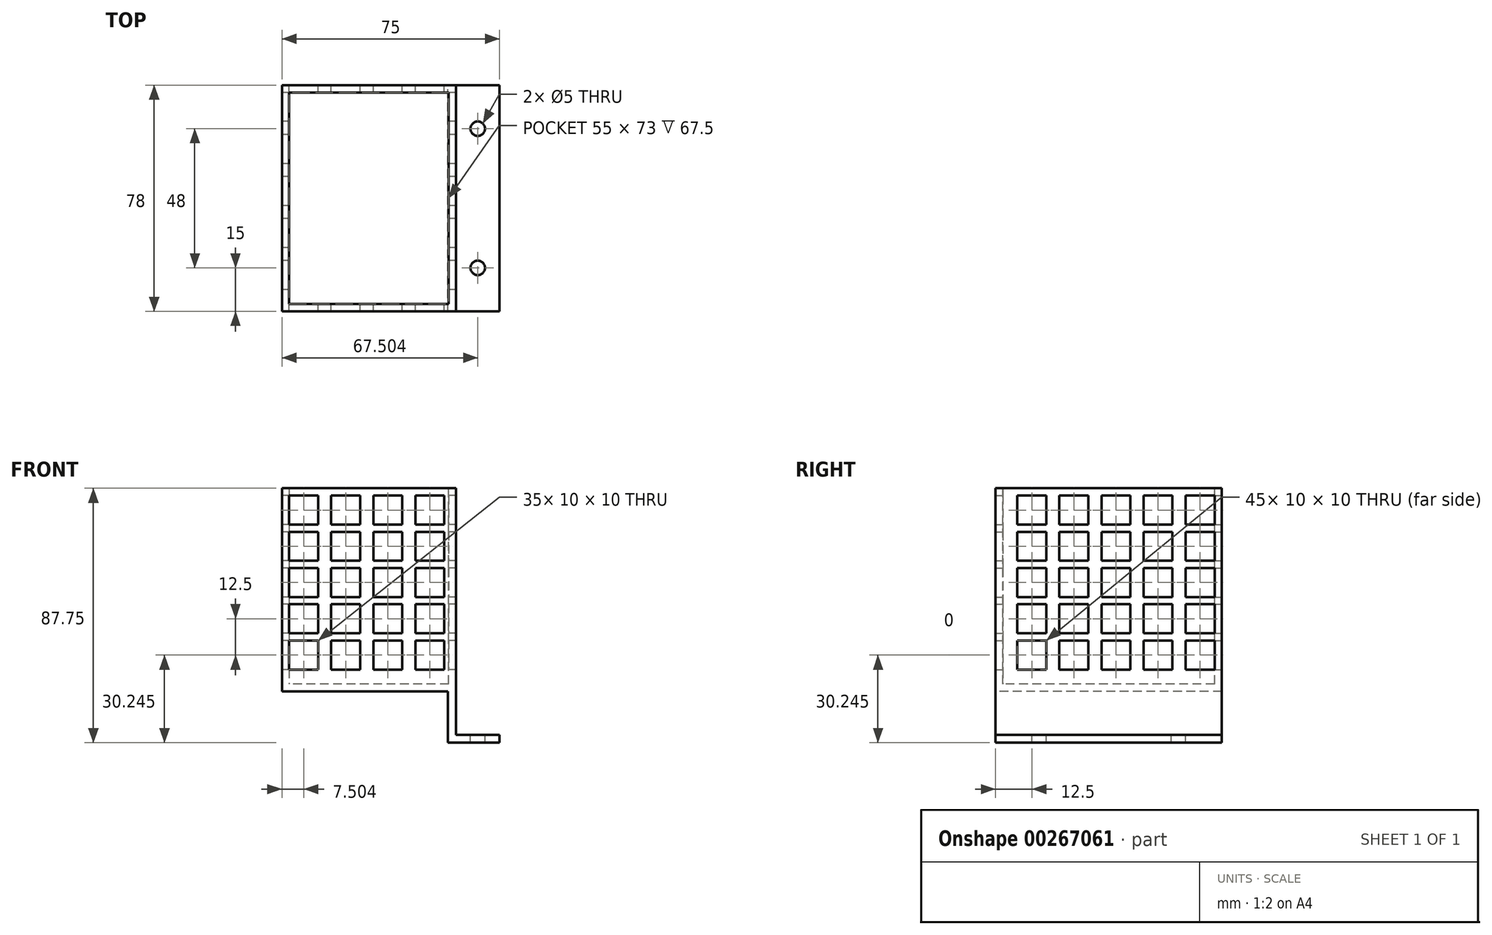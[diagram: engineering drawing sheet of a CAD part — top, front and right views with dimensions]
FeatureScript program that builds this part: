
annotation { "Feature Type Name" : "Feature", "Feature Type Description" : "" }
export const myFeature = defineFeature(function(context is Context, id is Id, definition is map)
    precondition{}
    {
        {
            var Q0;
            Q0=qCreatedBy(makeId("Front.planeOp"),FACE);
            var sketch = newSketch(context, id + "F0", { "sketchPlane" : qUnion([Q0])});
            skLineSegment(sketch, "E0", {"start": v(29.8, 18.38) * mm, "end": v(44.8, 18.38) * mm});
            skLineSegment(sketch, "E1", {"start": v(44.8, 18.38) * mm, "end": v(44.8, 21.13) * mm});
            skLineSegment(sketch, "E2", {"start": v(44.8, 21.13) * mm, "end": v(29.8, 21.13) * mm});
            skLineSegment(sketch, "E3", {"start": v(29.8, 21.13) * mm, "end": v(29.8, 18.38) * mm});
            skLineSegment(sketch, "E4.bottom", {"start": v(29.8, 18.38) * mm, "end": v(27.04, 18.38) * mm});
            skLineSegment(sketch, "E4.top", {"start": v(29.8, 36.13) * mm, "end": v(27.04, 36.13) * mm});
            skLineSegment(sketch, "E4.left", {"start": v(29.8, 18.38) * mm, "end": v(29.8, 36.13) * mm});
            skLineSegment(sketch, "E4.right", {"start": v(27.04, 18.38) * mm, "end": v(27.04, 36.13) * mm});
            skSolve(sketch);
        }
        {
            var Q0;
            Q0=qSketchRegion(id+"F0",true);
            extrude(context, id + "F1", {"entities" : qUnion([Q0]), "endBound" : BoundingType.SYMMETRIC, "depth" : 78 * mm});
        }
        {
            var Q0;
            Q0=makeQuery(id+"F1.opExtrude","SWEPT_FACE",FACE,{"disambiguationData":[OSD([sQuery(id+"F0.wireOp",EDGE,"E2")])]});
            var sketch = newSketch(context, id + "F2", { "sketchPlane" : qUnion([Q0])});
            skCircle(sketch, "E5", {"center": v(37.3, -24) * mm, "radius": 2.5 * mm});
            skCircle(sketch, "E6.0.1.0", {"center": v(37.3, 24) * mm, "radius": 2.5 * mm});
            skLineSegment(sketch, "E6.direction1", {"start": v(37.3, -24) * mm, "end": v(64.68, -24) * mm, "construction": true});
            skLineSegment(sketch, "E6.direction2", {"start": v(37.3, -24) * mm, "end": v(37.3, 24) * mm, "construction": true});
            skLineSegment(sketch, "E7.0", {"start": v(44.8, 39) * mm, "end": v(44.8, -39) * mm});
            skLineSegment(sketch, "E8.0", {"start": v(44.8, -39) * mm, "end": v(44.8, 39) * mm});
            skLineSegment(sketch, "E9", {"start": v(44.8, -1.08) * mm, "end": v(44.8, -1.08) * mm});
            skPoint(sketch, "E9.endSnap0", {"position": v(44.8, 0) * mm});
            skPoint(sketch, "E10", {"position": v(37.3, -1.08) * mm});
            skLineSegment(sketch, "E11", {"start": v(29.8, 0) * mm, "end": v(44.8, 0) * mm, "construction": true});
            skPoint(sketch, "E12", {"position": v(37.3, 0) * mm});
            skSolve(sketch);
        }
        {
            var Q0;
            Q0=makeQuery(id+"F2.imprint","IMPRINT",FACE,{"disambiguationData":[TD([[makeQuery(id+"F2.imprint","IMPRINT",EDGE,{"derivedFrom":sQuery(id+"F2.wireOp",EDGE,"E6.0.1.0")}),1.0]])]});
            var Q1;
            Q1=makeQuery(id+"F2.imprint","IMPRINT",FACE,{"disambiguationData":[TD([[makeQuery(id+"F2.imprint","IMPRINT",EDGE,{"derivedFrom":sQuery(id+"F2.wireOp",EDGE,"E5")}),1.0]])]});
            extrude(context, id + "F3", {"entities" : qUnion([Q0, Q1]), "operationType" : NewBodyOperationType.REMOVE, "endBound" : BoundingType.THROUGH_ALL, "oppositeDirection" : true, "depth" : 25 * mm});
        }
        {
            var Q0;
            Q0=makeQuery(id+"F1.opExtrude","SWEPT_FACE",FACE,{"disambiguationData":[OSD([sQuery(id+"F0.wireOp",EDGE,"E4.top")])]});
            var sketch = newSketch(context, id + "F4", { "sketchPlane" : qUnion([Q0])});
            skLineSegment(sketch, "E13", {"start": v(29.8, 39) * mm, "end": v(-30.2, 39) * mm});
            skLineSegment(sketch, "E14", {"start": v(29.8, -39) * mm, "end": v(-30.2, -39) * mm});
            skLineSegment(sketch, "E15", {"start": v(-30.2, 39) * mm, "end": v(-30.2, -39) * mm});
            skSolve(sketch);
        }
        {
            var Q0;
            {var subQ0=sQuery(id+"F4.wireOp",EDGE,"E13");Q0=makeQuery(id+"F4.imprint","IMPRINT",FACE,{"disambiguationData":[TD([[makeQuery(id+"F4.imprint","IMPRINT",EDGE,{"derivedFrom":subQ0}),1.0]])]});}
            extrude(context, id + "F5", {"entities" : qUnion([Q0]), "operationType" : NewBodyOperationType.ADD, "depth" : 70 * mm});
        }
        {
            var Q0;
            Q0=makeQuery(id+"F5.opExtrude","CAP_FACE",FACE,{"disambiguationData":[OSD([sQuery(id+"F0.wireOp",EDGE,"E0"),sQuery(id+"F0.wireOp",EDGE,"E3"),sQuery(id+"F4.wireOp",EDGE,"E13"),sQuery(id+"F4.wireOp",EDGE,"E14"),sQuery(id+"F4.wireOp",EDGE,"XroIyZZh-nZdX-ji37-o0S8-ZtPrHTp5OUbo")])],"isStart":false});
            shell(context, id + "F6", {"entities" : qUnion([Q0]), "thickness" : 2.5 * mm});
        }
        {
            var Q0;
            Q0=makeQuery(id+"F5.opExtrude","SWEPT_FACE",FACE,{"disambiguationData":[OSD([sQuery(id+"F4.wireOp",EDGE,"E13")])]});
            var sketch = newSketch(context, id + "F7", { "sketchPlane" : qUnion([Q0])});
            skLineSegment(sketch, "E16.bottom", {"start": v(17.7, 103.63) * mm, "end": v(27.7, 103.63) * mm});
            skLineSegment(sketch, "E16.top", {"start": v(17.7, 93.63) * mm, "end": v(27.7, 93.63) * mm});
            skLineSegment(sketch, "E16.left", {"start": v(27.7, 93.63) * mm, "end": v(27.7, 103.63) * mm});
            skLineSegment(sketch, "E16.right", {"start": v(17.7, 93.63) * mm, "end": v(17.7, 103.63) * mm});
            skLineSegment(sketch, "E17.0.1.0", {"start": v(17.7, 91.13) * mm, "end": v(27.7, 91.13) * mm});
            skLineSegment(sketch, "E17.0.1.1", {"start": v(27.7, 81.13) * mm, "end": v(27.7, 91.13) * mm});
            skLineSegment(sketch, "E17.0.1.2", {"start": v(17.7, 81.13) * mm, "end": v(17.7, 91.13) * mm});
            skLineSegment(sketch, "E17.0.1.3", {"start": v(17.7, 81.13) * mm, "end": v(27.7, 81.13) * mm});
            skLineSegment(sketch, "E17.0.2.0", {"start": v(17.7, 78.63) * mm, "end": v(27.7, 78.63) * mm});
            skLineSegment(sketch, "E17.0.2.1", {"start": v(27.7, 68.63) * mm, "end": v(27.7, 78.63) * mm});
            skLineSegment(sketch, "E17.0.2.2", {"start": v(17.7, 68.63) * mm, "end": v(17.7, 78.63) * mm});
            skLineSegment(sketch, "E17.0.2.3", {"start": v(17.7, 68.63) * mm, "end": v(27.7, 68.63) * mm});
            skLineSegment(sketch, "E17.0.3.0", {"start": v(17.7, 66.13) * mm, "end": v(27.7, 66.13) * mm});
            skLineSegment(sketch, "E17.0.3.1", {"start": v(27.7, 56.13) * mm, "end": v(27.7, 66.13) * mm});
            skLineSegment(sketch, "E17.0.3.2", {"start": v(17.7, 56.13) * mm, "end": v(17.7, 66.13) * mm});
            skLineSegment(sketch, "E17.0.3.3", {"start": v(17.7, 56.13) * mm, "end": v(27.7, 56.13) * mm});
            skLineSegment(sketch, "E17.0.4.0", {"start": v(17.7, 53.63) * mm, "end": v(27.7, 53.63) * mm});
            skLineSegment(sketch, "E17.0.4.1", {"start": v(27.7, 43.63) * mm, "end": v(27.7, 53.63) * mm});
            skLineSegment(sketch, "E17.0.4.2", {"start": v(17.7, 43.63) * mm, "end": v(17.7, 53.63) * mm});
            skLineSegment(sketch, "E17.0.4.3", {"start": v(17.7, 43.63) * mm, "end": v(27.7, 43.63) * mm});
            skLineSegment(sketch, "E18.1.0.0", {"start": v(3.2, 93.63) * mm, "end": v(3.2, 103.63) * mm});
            skLineSegment(sketch, "E18.1.0.1", {"start": v(3.2, 93.63) * mm, "end": v(13.2, 93.63) * mm});
            skLineSegment(sketch, "E18.1.0.2", {"start": v(3.2, 103.63) * mm, "end": v(13.2, 103.63) * mm});
            skLineSegment(sketch, "E18.1.0.3", {"start": v(13.2, 93.63) * mm, "end": v(13.2, 103.63) * mm});
            skLineSegment(sketch, "E18.1.1.0", {"start": v(3.2, 81.13) * mm, "end": v(3.2, 91.13) * mm});
            skLineSegment(sketch, "E18.1.1.1", {"start": v(3.2, 81.13) * mm, "end": v(13.2, 81.13) * mm});
            skLineSegment(sketch, "E18.1.1.2", {"start": v(3.2, 91.13) * mm, "end": v(13.2, 91.13) * mm});
            skLineSegment(sketch, "E18.1.1.3", {"start": v(13.2, 81.13) * mm, "end": v(13.2, 91.13) * mm});
            skLineSegment(sketch, "E18.1.2.0", {"start": v(3.2, 68.63) * mm, "end": v(3.2, 78.63) * mm});
            skLineSegment(sketch, "E18.1.2.1", {"start": v(3.2, 68.63) * mm, "end": v(13.2, 68.63) * mm});
            skLineSegment(sketch, "E18.1.2.2", {"start": v(3.2, 78.63) * mm, "end": v(13.2, 78.63) * mm});
            skLineSegment(sketch, "E18.1.2.3", {"start": v(13.2, 68.63) * mm, "end": v(13.2, 78.63) * mm});
            skLineSegment(sketch, "E18.1.3.0", {"start": v(3.2, 56.13) * mm, "end": v(3.2, 66.13) * mm});
            skLineSegment(sketch, "E18.1.3.1", {"start": v(3.2, 56.13) * mm, "end": v(13.2, 56.13) * mm});
            skLineSegment(sketch, "E18.1.3.2", {"start": v(3.2, 66.13) * mm, "end": v(13.2, 66.13) * mm});
            skLineSegment(sketch, "E18.1.3.3", {"start": v(13.2, 56.13) * mm, "end": v(13.2, 66.13) * mm});
            skLineSegment(sketch, "E18.1.4.0", {"start": v(3.2, 43.63) * mm, "end": v(3.2, 53.63) * mm});
            skLineSegment(sketch, "E18.1.4.1", {"start": v(3.2, 43.63) * mm, "end": v(13.2, 43.63) * mm});
            skLineSegment(sketch, "E18.1.4.2", {"start": v(3.2, 53.63) * mm, "end": v(13.2, 53.63) * mm});
            skLineSegment(sketch, "E18.1.4.3", {"start": v(13.2, 43.63) * mm, "end": v(13.2, 53.63) * mm});
            skLineSegment(sketch, "E18.2.0.0", {"start": v(-11.3, 93.63) * mm, "end": v(-11.3, 103.63) * mm});
            skLineSegment(sketch, "E18.2.0.1", {"start": v(-11.3, 93.63) * mm, "end": v(-1.3, 93.63) * mm});
            skLineSegment(sketch, "E18.2.0.2", {"start": v(-11.3, 103.63) * mm, "end": v(-1.3, 103.63) * mm});
            skLineSegment(sketch, "E18.2.0.3", {"start": v(-1.3, 93.63) * mm, "end": v(-1.3, 103.63) * mm});
            skLineSegment(sketch, "E18.2.1.0", {"start": v(-11.3, 81.13) * mm, "end": v(-11.3, 91.13) * mm});
            skLineSegment(sketch, "E18.2.1.1", {"start": v(-11.3, 81.13) * mm, "end": v(-1.3, 81.13) * mm});
            skLineSegment(sketch, "E18.2.1.2", {"start": v(-11.3, 91.13) * mm, "end": v(-1.3, 91.13) * mm});
            skLineSegment(sketch, "E18.2.1.3", {"start": v(-1.3, 81.13) * mm, "end": v(-1.3, 91.13) * mm});
            skLineSegment(sketch, "E18.2.2.0", {"start": v(-11.3, 68.63) * mm, "end": v(-11.3, 78.63) * mm});
            skLineSegment(sketch, "E18.2.2.1", {"start": v(-11.3, 68.63) * mm, "end": v(-1.3, 68.63) * mm});
            skLineSegment(sketch, "E18.2.2.2", {"start": v(-11.3, 78.63) * mm, "end": v(-1.3, 78.63) * mm});
            skLineSegment(sketch, "E18.2.2.3", {"start": v(-1.3, 68.63) * mm, "end": v(-1.3, 78.63) * mm});
            skLineSegment(sketch, "E18.2.3.0", {"start": v(-11.3, 56.13) * mm, "end": v(-11.3, 66.13) * mm});
            skLineSegment(sketch, "E18.2.3.1", {"start": v(-11.3, 56.13) * mm, "end": v(-1.3, 56.13) * mm});
            skLineSegment(sketch, "E18.2.3.2", {"start": v(-11.3, 66.13) * mm, "end": v(-1.3, 66.13) * mm});
            skLineSegment(sketch, "E18.2.3.3", {"start": v(-1.3, 56.13) * mm, "end": v(-1.3, 66.13) * mm});
            skLineSegment(sketch, "E18.2.4.0", {"start": v(-11.3, 43.63) * mm, "end": v(-11.3, 53.63) * mm});
            skLineSegment(sketch, "E18.2.4.1", {"start": v(-11.3, 43.63) * mm, "end": v(-1.3, 43.63) * mm});
            skLineSegment(sketch, "E18.2.4.2", {"start": v(-11.3, 53.63) * mm, "end": v(-1.3, 53.63) * mm});
            skLineSegment(sketch, "E18.2.4.3", {"start": v(-1.3, 43.63) * mm, "end": v(-1.3, 53.63) * mm});
            skLineSegment(sketch, "E18.3.0.0", {"start": v(-25.8, 93.63) * mm, "end": v(-25.8, 103.63) * mm});
            skLineSegment(sketch, "E18.3.0.1", {"start": v(-25.8, 93.63) * mm, "end": v(-15.8, 93.63) * mm});
            skLineSegment(sketch, "E18.3.0.2", {"start": v(-25.8, 103.63) * mm, "end": v(-15.8, 103.63) * mm});
            skLineSegment(sketch, "E18.3.0.3", {"start": v(-15.8, 93.63) * mm, "end": v(-15.8, 103.63) * mm});
            skLineSegment(sketch, "E18.3.1.0", {"start": v(-25.8, 81.13) * mm, "end": v(-25.8, 91.13) * mm});
            skLineSegment(sketch, "E18.3.1.1", {"start": v(-25.8, 81.13) * mm, "end": v(-15.8, 81.13) * mm});
            skLineSegment(sketch, "E18.3.1.2", {"start": v(-25.8, 91.13) * mm, "end": v(-15.8, 91.13) * mm});
            skLineSegment(sketch, "E18.3.1.3", {"start": v(-15.8, 81.13) * mm, "end": v(-15.8, 91.13) * mm});
            skLineSegment(sketch, "E18.3.2.0", {"start": v(-25.8, 68.63) * mm, "end": v(-25.8, 78.63) * mm});
            skLineSegment(sketch, "E18.3.2.1", {"start": v(-25.8, 68.63) * mm, "end": v(-15.8, 68.63) * mm});
            skLineSegment(sketch, "E18.3.2.2", {"start": v(-25.8, 78.63) * mm, "end": v(-15.8, 78.63) * mm});
            skLineSegment(sketch, "E18.3.2.3", {"start": v(-15.8, 68.63) * mm, "end": v(-15.8, 78.63) * mm});
            skLineSegment(sketch, "E18.3.3.0", {"start": v(-25.8, 56.13) * mm, "end": v(-25.8, 66.13) * mm});
            skLineSegment(sketch, "E18.3.3.1", {"start": v(-25.8, 56.13) * mm, "end": v(-15.8, 56.13) * mm});
            skLineSegment(sketch, "E18.3.3.2", {"start": v(-25.8, 66.13) * mm, "end": v(-15.8, 66.13) * mm});
            skLineSegment(sketch, "E18.3.3.3", {"start": v(-15.8, 56.13) * mm, "end": v(-15.8, 66.13) * mm});
            skLineSegment(sketch, "E18.3.4.0", {"start": v(-25.8, 43.63) * mm, "end": v(-25.8, 53.63) * mm});
            skLineSegment(sketch, "E18.3.4.1", {"start": v(-25.8, 43.63) * mm, "end": v(-15.8, 43.63) * mm});
            skLineSegment(sketch, "E18.3.4.2", {"start": v(-25.8, 53.63) * mm, "end": v(-15.8, 53.63) * mm});
            skLineSegment(sketch, "E18.3.4.3", {"start": v(-15.8, 43.63) * mm, "end": v(-15.8, 53.63) * mm});
            skLineSegment(sketch, "E18.direction1", {"start": v(17.7, 93.63) * mm, "end": v(3.2, 93.63) * mm, "construction": true});
            skLineSegment(sketch, "E18.direction2", {"start": v(17.7, 93.63) * mm, "end": v(17.7, 81.13) * mm, "construction": true});
            skSolve(sketch);
        }
        {
            var Q0;
            Q0 = qSketchRegion(id + "F7", true);
            extrude(context, id + "F8", {"entities" : qUnion([Q0]), "operationType" : NewBodyOperationType.REMOVE, "endBound" : BoundingType.THROUGH_ALL, "oppositeDirection" : true, "depth" : 25 * mm});
        }
        {
            var Q0;
            Q0=makeQuery(id+"F5.opExtrude","SWEPT_FACE",FACE,{"disambiguationData":[OSD([sQuery(id+"F4.wireOp",EDGE,"E15")])]});
            var sketch = newSketch(context, id + "F9", { "sketchPlane" : qUnion([Q0])});
            skLineSegment(sketch, "E19.bottom", {"start": v(-36.5, 103.63) * mm, "end": v(-26.5, 103.63) * mm});
            skLineSegment(sketch, "E19.top", {"start": v(-36.5, 93.63) * mm, "end": v(-26.5, 93.63) * mm});
            skLineSegment(sketch, "E19.left", {"start": v(-36.5, 103.63) * mm, "end": v(-36.5, 93.63) * mm});
            skLineSegment(sketch, "E19.right", {"start": v(-26.5, 103.63) * mm, "end": v(-26.5, 93.63) * mm});
            skLineSegment(sketch, "E20.0.1.0", {"start": v(-36.5, 91.13) * mm, "end": v(-36.5, 81.13) * mm});
            skLineSegment(sketch, "E20.0.1.1", {"start": v(-36.5, 91.13) * mm, "end": v(-26.5, 91.13) * mm});
            skLineSegment(sketch, "E20.0.1.2", {"start": v(-26.5, 91.13) * mm, "end": v(-26.5, 81.13) * mm});
            skLineSegment(sketch, "E20.0.1.3", {"start": v(-36.5, 81.13) * mm, "end": v(-26.5, 81.13) * mm});
            skLineSegment(sketch, "E20.0.2.0", {"start": v(-36.5, 78.63) * mm, "end": v(-36.5, 68.63) * mm});
            skLineSegment(sketch, "E20.0.2.1", {"start": v(-36.5, 78.63) * mm, "end": v(-26.5, 78.63) * mm});
            skLineSegment(sketch, "E20.0.2.2", {"start": v(-26.5, 78.63) * mm, "end": v(-26.5, 68.63) * mm});
            skLineSegment(sketch, "E20.0.2.3", {"start": v(-36.5, 68.63) * mm, "end": v(-26.5, 68.63) * mm});
            skLineSegment(sketch, "E20.0.3.0", {"start": v(-36.5, 66.13) * mm, "end": v(-36.5, 56.13) * mm});
            skLineSegment(sketch, "E20.0.3.1", {"start": v(-36.5, 66.13) * mm, "end": v(-26.5, 66.13) * mm});
            skLineSegment(sketch, "E20.0.3.2", {"start": v(-26.5, 66.13) * mm, "end": v(-26.5, 56.13) * mm});
            skLineSegment(sketch, "E20.0.3.3", {"start": v(-36.5, 56.13) * mm, "end": v(-26.5, 56.13) * mm});
            skLineSegment(sketch, "E20.0.4.0", {"start": v(-36.5, 53.63) * mm, "end": v(-36.5, 43.63) * mm});
            skLineSegment(sketch, "E20.0.4.1", {"start": v(-36.5, 53.63) * mm, "end": v(-26.5, 53.63) * mm});
            skLineSegment(sketch, "E20.0.4.2", {"start": v(-26.5, 53.63) * mm, "end": v(-26.5, 43.63) * mm});
            skLineSegment(sketch, "E20.0.4.3", {"start": v(-36.5, 43.63) * mm, "end": v(-26.5, 43.63) * mm});
            skLineSegment(sketch, "E20.1.0.0", {"start": v(-22, 103.63) * mm, "end": v(-22, 93.63) * mm});
            skLineSegment(sketch, "E20.1.0.1", {"start": v(-22, 103.63) * mm, "end": v(-12, 103.63) * mm});
            skLineSegment(sketch, "E20.1.0.2", {"start": v(-12, 103.63) * mm, "end": v(-12, 93.63) * mm});
            skLineSegment(sketch, "E20.1.0.3", {"start": v(-22, 93.63) * mm, "end": v(-12, 93.63) * mm});
            skLineSegment(sketch, "E20.1.1.0", {"start": v(-22, 91.13) * mm, "end": v(-22, 81.13) * mm});
            skLineSegment(sketch, "E20.1.1.1", {"start": v(-22, 91.13) * mm, "end": v(-12, 91.13) * mm});
            skLineSegment(sketch, "E20.1.1.2", {"start": v(-12, 91.13) * mm, "end": v(-12, 81.13) * mm});
            skLineSegment(sketch, "E20.1.1.3", {"start": v(-22, 81.13) * mm, "end": v(-12, 81.13) * mm});
            skLineSegment(sketch, "E20.1.2.0", {"start": v(-22, 78.63) * mm, "end": v(-22, 68.63) * mm});
            skLineSegment(sketch, "E20.1.2.1", {"start": v(-22, 78.63) * mm, "end": v(-12, 78.63) * mm});
            skLineSegment(sketch, "E20.1.2.2", {"start": v(-12, 78.63) * mm, "end": v(-12, 68.63) * mm});
            skLineSegment(sketch, "E20.1.2.3", {"start": v(-22, 68.63) * mm, "end": v(-12, 68.63) * mm});
            skLineSegment(sketch, "E20.1.3.0", {"start": v(-22, 66.13) * mm, "end": v(-22, 56.13) * mm});
            skLineSegment(sketch, "E20.1.3.1", {"start": v(-22, 66.13) * mm, "end": v(-12, 66.13) * mm});
            skLineSegment(sketch, "E20.1.3.2", {"start": v(-12, 66.13) * mm, "end": v(-12, 56.13) * mm});
            skLineSegment(sketch, "E20.1.3.3", {"start": v(-22, 56.13) * mm, "end": v(-12, 56.13) * mm});
            skLineSegment(sketch, "E20.1.4.0", {"start": v(-22, 53.63) * mm, "end": v(-22, 43.63) * mm});
            skLineSegment(sketch, "E20.1.4.1", {"start": v(-22, 53.63) * mm, "end": v(-12, 53.63) * mm});
            skLineSegment(sketch, "E20.1.4.2", {"start": v(-12, 53.63) * mm, "end": v(-12, 43.63) * mm});
            skLineSegment(sketch, "E20.1.4.3", {"start": v(-22, 43.63) * mm, "end": v(-12, 43.63) * mm});
            skLineSegment(sketch, "E20.2.0.0", {"start": v(-7.5, 103.63) * mm, "end": v(-7.5, 93.63) * mm});
            skLineSegment(sketch, "E20.2.0.1", {"start": v(-7.5, 103.63) * mm, "end": v(2.5, 103.63) * mm});
            skLineSegment(sketch, "E20.2.0.2", {"start": v(2.5, 103.63) * mm, "end": v(2.5, 93.63) * mm});
            skLineSegment(sketch, "E20.2.0.3", {"start": v(-7.5, 93.63) * mm, "end": v(2.5, 93.63) * mm});
            skLineSegment(sketch, "E20.2.1.0", {"start": v(-7.5, 91.13) * mm, "end": v(-7.5, 81.13) * mm});
            skLineSegment(sketch, "E20.2.1.1", {"start": v(-7.5, 91.13) * mm, "end": v(2.5, 91.13) * mm});
            skLineSegment(sketch, "E20.2.1.2", {"start": v(2.5, 91.13) * mm, "end": v(2.5, 81.13) * mm});
            skLineSegment(sketch, "E20.2.1.3", {"start": v(-7.5, 81.13) * mm, "end": v(2.5, 81.13) * mm});
            skLineSegment(sketch, "E20.2.2.0", {"start": v(-7.5, 78.63) * mm, "end": v(-7.5, 68.63) * mm});
            skLineSegment(sketch, "E20.2.2.1", {"start": v(-7.5, 78.63) * mm, "end": v(2.5, 78.63) * mm});
            skLineSegment(sketch, "E20.2.2.2", {"start": v(2.5, 78.63) * mm, "end": v(2.5, 68.63) * mm});
            skLineSegment(sketch, "E20.2.2.3", {"start": v(-7.5, 68.63) * mm, "end": v(2.5, 68.63) * mm});
            skLineSegment(sketch, "E20.2.3.0", {"start": v(-7.5, 66.13) * mm, "end": v(-7.5, 56.13) * mm});
            skLineSegment(sketch, "E20.2.3.1", {"start": v(-7.5, 66.13) * mm, "end": v(2.5, 66.13) * mm});
            skLineSegment(sketch, "E20.2.3.2", {"start": v(2.5, 66.13) * mm, "end": v(2.5, 56.13) * mm});
            skLineSegment(sketch, "E20.2.3.3", {"start": v(-7.5, 56.13) * mm, "end": v(2.5, 56.13) * mm});
            skLineSegment(sketch, "E20.2.4.0", {"start": v(-7.5, 53.63) * mm, "end": v(-7.5, 43.63) * mm});
            skLineSegment(sketch, "E20.2.4.1", {"start": v(-7.5, 53.63) * mm, "end": v(2.5, 53.63) * mm});
            skLineSegment(sketch, "E20.2.4.2", {"start": v(2.5, 53.63) * mm, "end": v(2.5, 43.63) * mm});
            skLineSegment(sketch, "E20.2.4.3", {"start": v(-7.5, 43.63) * mm, "end": v(2.5, 43.63) * mm});
            skLineSegment(sketch, "E20.3.0.0", {"start": v(7, 103.63) * mm, "end": v(7, 93.63) * mm});
            skLineSegment(sketch, "E20.3.0.1", {"start": v(7, 103.63) * mm, "end": v(17, 103.63) * mm});
            skLineSegment(sketch, "E20.3.0.2", {"start": v(17, 103.63) * mm, "end": v(17, 93.63) * mm});
            skLineSegment(sketch, "E20.3.0.3", {"start": v(7, 93.63) * mm, "end": v(17, 93.63) * mm});
            skLineSegment(sketch, "E20.3.1.0", {"start": v(7, 91.13) * mm, "end": v(7, 81.13) * mm});
            skLineSegment(sketch, "E20.3.1.1", {"start": v(7, 91.13) * mm, "end": v(17, 91.13) * mm});
            skLineSegment(sketch, "E20.3.1.2", {"start": v(17, 91.13) * mm, "end": v(17, 81.13) * mm});
            skLineSegment(sketch, "E20.3.1.3", {"start": v(7, 81.13) * mm, "end": v(17, 81.13) * mm});
            skLineSegment(sketch, "E20.3.2.0", {"start": v(7, 78.63) * mm, "end": v(7, 68.63) * mm});
            skLineSegment(sketch, "E20.3.2.1", {"start": v(7, 78.63) * mm, "end": v(17, 78.63) * mm});
            skLineSegment(sketch, "E20.3.2.2", {"start": v(17, 78.63) * mm, "end": v(17, 68.63) * mm});
            skLineSegment(sketch, "E20.3.2.3", {"start": v(7, 68.63) * mm, "end": v(17, 68.63) * mm});
            skLineSegment(sketch, "E20.3.3.0", {"start": v(7, 66.13) * mm, "end": v(7, 56.13) * mm});
            skLineSegment(sketch, "E20.3.3.1", {"start": v(7, 66.13) * mm, "end": v(17, 66.13) * mm});
            skLineSegment(sketch, "E20.3.3.2", {"start": v(17, 66.13) * mm, "end": v(17, 56.13) * mm});
            skLineSegment(sketch, "E20.3.3.3", {"start": v(7, 56.13) * mm, "end": v(17, 56.13) * mm});
            skLineSegment(sketch, "E20.3.4.0", {"start": v(7, 53.63) * mm, "end": v(7, 43.63) * mm});
            skLineSegment(sketch, "E20.3.4.1", {"start": v(7, 53.63) * mm, "end": v(17, 53.63) * mm});
            skLineSegment(sketch, "E20.3.4.2", {"start": v(17, 53.63) * mm, "end": v(17, 43.63) * mm});
            skLineSegment(sketch, "E20.3.4.3", {"start": v(7, 43.63) * mm, "end": v(17, 43.63) * mm});
            skLineSegment(sketch, "E20.direction1", {"start": v(-36.5, 93.63) * mm, "end": v(-22, 93.63) * mm, "construction": true});
            skLineSegment(sketch, "E20.direction2", {"start": v(-36.5, 93.63) * mm, "end": v(-36.5, 81.13) * mm, "construction": true});
            skLineSegment(sketch, "E21.0.4.0", {"start": v(21.5, 103.63) * mm, "end": v(21.5, 93.63) * mm});
            skLineSegment(sketch, "E21.3.4.0", {"start": v(21.5, 103.63) * mm, "end": v(31.5, 103.63) * mm});
            skLineSegment(sketch, "E21.6.4.0", {"start": v(31.5, 103.63) * mm, "end": v(31.5, 93.63) * mm});
            skLineSegment(sketch, "E21.9.4.0", {"start": v(21.5, 93.63) * mm, "end": v(31.5, 93.63) * mm});
            skLineSegment(sketch, "E21.0.4.1", {"start": v(21.5, 91.13) * mm, "end": v(21.5, 81.13) * mm});
            skLineSegment(sketch, "E21.3.4.1", {"start": v(21.5, 91.13) * mm, "end": v(31.5, 91.13) * mm});
            skLineSegment(sketch, "E21.6.4.1", {"start": v(31.5, 91.13) * mm, "end": v(31.5, 81.13) * mm});
            skLineSegment(sketch, "E21.9.4.1", {"start": v(21.5, 81.13) * mm, "end": v(31.5, 81.13) * mm});
            skLineSegment(sketch, "E21.0.4.2", {"start": v(21.5, 78.63) * mm, "end": v(21.5, 68.63) * mm});
            skLineSegment(sketch, "E21.3.4.2", {"start": v(21.5, 78.63) * mm, "end": v(31.5, 78.63) * mm});
            skLineSegment(sketch, "E21.6.4.2", {"start": v(31.5, 78.63) * mm, "end": v(31.5, 68.63) * mm});
            skLineSegment(sketch, "E21.9.4.2", {"start": v(21.5, 68.63) * mm, "end": v(31.5, 68.63) * mm});
            skLineSegment(sketch, "E21.0.4.3", {"start": v(21.5, 66.13) * mm, "end": v(21.5, 56.13) * mm});
            skLineSegment(sketch, "E21.3.4.3", {"start": v(21.5, 66.13) * mm, "end": v(31.5, 66.13) * mm});
            skLineSegment(sketch, "E21.6.4.3", {"start": v(31.5, 66.13) * mm, "end": v(31.5, 56.13) * mm});
            skLineSegment(sketch, "E21.9.4.3", {"start": v(21.5, 56.13) * mm, "end": v(31.5, 56.13) * mm});
            skLineSegment(sketch, "E21.0.4.4", {"start": v(21.5, 53.63) * mm, "end": v(21.5, 43.63) * mm});
            skLineSegment(sketch, "E21.3.4.4", {"start": v(21.5, 53.63) * mm, "end": v(31.5, 53.63) * mm});
            skLineSegment(sketch, "E21.6.4.4", {"start": v(31.5, 53.63) * mm, "end": v(31.5, 43.63) * mm});
            skLineSegment(sketch, "E21.9.4.4", {"start": v(21.5, 43.63) * mm, "end": v(31.5, 43.63) * mm});
            skSolve(sketch);
        }
        {
            var Q0;
            Q0 = qSketchRegion(id + "F9", true);
            extrude(context, id + "F10", {"entities" : qUnion([Q0]), "operationType" : NewBodyOperationType.REMOVE, "endBound" : BoundingType.THROUGH_ALL, "oppositeDirection" : true, "depth" : 25 * mm});
        }
    });
